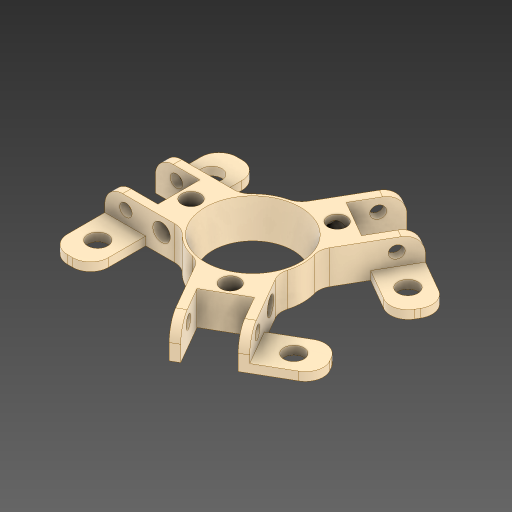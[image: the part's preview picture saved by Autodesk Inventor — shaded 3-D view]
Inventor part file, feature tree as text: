
AUTODESK INVENTOR PART (.ipt)
format: ipt  version: 2024 (Build 280153000, 153)  size: 620,544 bytes
history: native  units: in
note: dims shown in document units (in); Inventor stores cm internally (conversion verified against a paired STEP export)
features: sketch x4, hole x3, extrude x2, pattern_circular x2, other x1, fillet x1, draft x1, projected_geometry x1
ambient origin geometry x8: Origin, YZ Plane, XZ Plane, XY Plane, X Axis, Y Axis, Z Axis, Center Point
bodies: Solid1 (feature_tree)
feature tree (15):
  other  "Nut/Rod Template"
  extrude  "Spring Holder"  Depth=0.2618in
  hole  "Spring Pin Hole"  [1 undecoded]
  pattern_circular  "Pin Pattern"  [2 undecoded]
  extrude  "Plate"  Depth=0.25in
  hole  "MNTG Holes"  [1 undecoded]
  fillet  ".25" Filet"  Radius=1.6in
  hole  "Set Screw Holes"  [1 undecoded]
  draft  "FaceDraft1"
  pattern_circular  "Circular Pattern2"  [2 undecoded]
  sketch  "Sketch2"  dims[d6=0.8661in d10=0.2618in]
  sketch  "Sketch5"  dims[d11=0.5906in d13=0.1703in]
  sketch  "Sketch12"  dims[d14=0.1181in]
  sketch  "Sketch14"  dims[d17=1.125in d18=0.625in d19=1.4in d20=1.1811in d22=360.0deg d24=1.6in d25=2.75in d26=0.4724in d27=0.0in d31=0.1732in d32=0.75in d33=0.375in d34=0.25in d35=0.5635in d36=1.0in d37=0.8108in d39=0.2953in d40=0.1772in d55=1.1811in d56=360.0deg d60=0.4493in d61=0.7874in d63=1.6in d64=0.7874in d66=2.75in d77=0.281in d78=0.75in d79=0.875in d80=0.25in d81=0.5635in d82=1.0in d83=0.8108in d93=0.0618in d94=0.0618in d95=0.1272in d96=0.1272in d97=0.0564in d99=0.1181in d100=0.0in d104=0.0564in d107=0.118in d108=0.118in d109=0.25in d111=0.2441in d112=0.315in d113=0.375in d114=0.25in d115=0.5635in d116=0.315in d117=0.0in d118=0.1969in d119=0.0859in d120=1.1811in d121=360.0deg]
  projected_geometry  "Projected Loop2"
note: 7 required parameter values undecoded (feature->parameter linkage not recoverable at this tier; creation-order binding heuristic only, values carry confidence <= 0.55)
